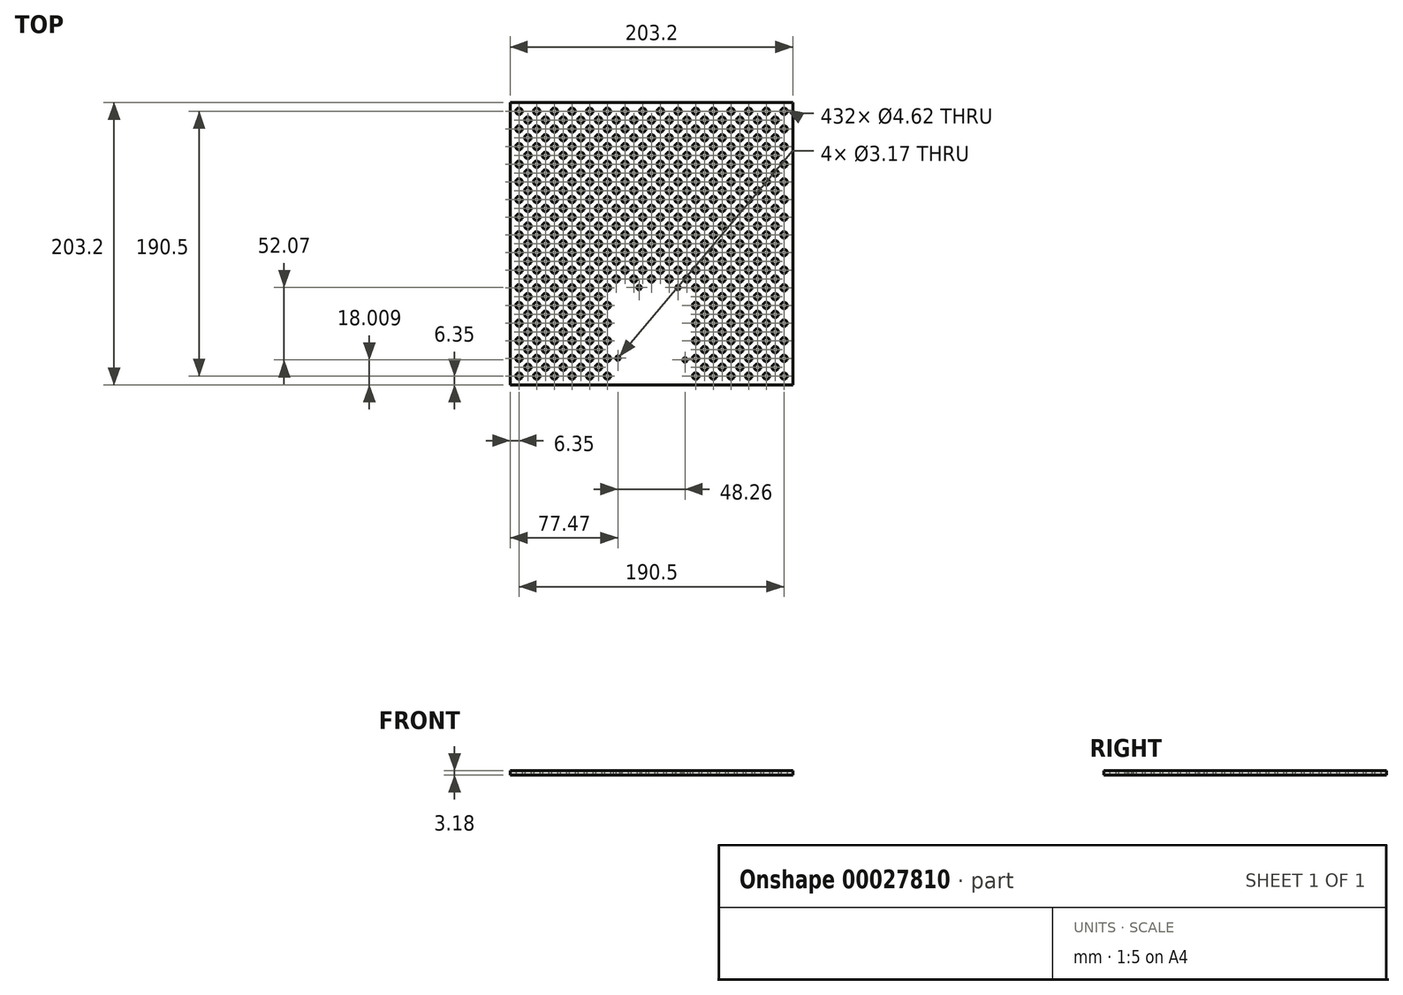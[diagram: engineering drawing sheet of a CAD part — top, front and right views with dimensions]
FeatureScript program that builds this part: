
annotation { "Feature Type Name" : "Feature", "Feature Type Description" : "" }
export const myFeature = defineFeature(function(context is Context, id is Id, definition is map)
    precondition{}
    {
        {
            var Q0;
            Q0=qCreatedBy(makeId("Top.planeOp"),FACE);
            var sketch = newSketch(context, id + "F0", { "sketchPlane" : qUnion([Q0])});
            skLineSegment(sketch, "E0", {"start": v(0, 0) * mm, "end": v(101.6, 0) * mm});
            skLineSegment(sketch, "E1", {"start": v(0, 0) * mm, "end": v(-101.6, 0) * mm});
            skLineSegment(sketch, "E2", {"start": v(-101.6, 0) * mm, "end": v(-101.6, 203.2) * mm});
            skLineSegment(sketch, "E3", {"start": v(101.6, 0) * mm, "end": v(101.6, 203.2) * mm});
            skLineSegment(sketch, "E4", {"start": v(-101.6, 203.2) * mm, "end": v(101.6, 203.2) * mm});
            skLineSegment(sketch, "E5", {"start": v(-101.6, 4.04) * mm, "end": v(101.6, 4.04) * mm, "construction": true});
            skLineSegment(sketch, "E6", {"start": v(0, 4.04) * mm, "end": v(-26.67, 4.04) * mm, "construction": true});
            skLineSegment(sketch, "E7", {"start": v(0, 4.04) * mm, "end": v(26.67, 4.04) * mm, "construction": true});
            skLineSegment(sketch, "E8", {"start": v(-101.6, 199.16) * mm, "end": v(101.6, 199.16) * mm, "construction": true});
            skLineSegment(sketch, "E9", {"start": v(-97.56, 203.2) * mm, "end": v(-97.56, 0) * mm, "construction": true});
            skCircle(sketch, "E10", {"center": v(-95.25, 196.85) * mm, "radius": 2.31 * mm});
            skCircle(sketch, "E11.0.1.0", {"center": v(-95.25, 184.15) * mm, "radius": 2.31 * mm});
            skCircle(sketch, "E11.0.2.0", {"center": v(-95.25, 171.45) * mm, "radius": 2.31 * mm});
            skCircle(sketch, "E11.0.3.0", {"center": v(-95.25, 158.75) * mm, "radius": 2.31 * mm});
            skCircle(sketch, "E11.0.4.0", {"center": v(-95.25, 146.05) * mm, "radius": 2.31 * mm});
            skCircle(sketch, "E11.0.5.0", {"center": v(-95.25, 133.35) * mm, "radius": 2.31 * mm});
            skCircle(sketch, "E11.0.6.0", {"center": v(-95.25, 120.65) * mm, "radius": 2.31 * mm});
            skCircle(sketch, "E11.0.7.0", {"center": v(-95.25, 107.95) * mm, "radius": 2.31 * mm});
            skCircle(sketch, "E11.0.8.0", {"center": v(-95.25, 95.25) * mm, "radius": 2.31 * mm});
            skCircle(sketch, "E11.0.9.0", {"center": v(-95.25, 82.55) * mm, "radius": 2.31 * mm});
            skCircle(sketch, "E11.0.10.0", {"center": v(-95.25, 69.85) * mm, "radius": 2.31 * mm});
            skCircle(sketch, "E11.0.11.0", {"center": v(-95.25, 57.15) * mm, "radius": 2.31 * mm});
            skCircle(sketch, "E11.0.12.0", {"center": v(-95.25, 44.45) * mm, "radius": 2.31 * mm});
            skCircle(sketch, "E11.0.13.0", {"center": v(-95.25, 31.75) * mm, "radius": 2.31 * mm});
            skCircle(sketch, "E11.0.14.0", {"center": v(-95.25, 19.05) * mm, "radius": 2.31 * mm});
            skCircle(sketch, "E11.0.15.0", {"center": v(-95.25, 6.35) * mm, "radius": 2.31 * mm});
            skCircle(sketch, "E11.1.0.0", {"center": v(-82.55, 196.85) * mm, "radius": 2.31 * mm});
            skCircle(sketch, "E11.1.1.0", {"center": v(-82.55, 184.15) * mm, "radius": 2.31 * mm});
            skCircle(sketch, "E11.1.2.0", {"center": v(-82.55, 171.45) * mm, "radius": 2.31 * mm});
            skCircle(sketch, "E11.1.3.0", {"center": v(-82.55, 158.75) * mm, "radius": 2.31 * mm});
            skCircle(sketch, "E11.1.4.0", {"center": v(-82.55, 146.05) * mm, "radius": 2.31 * mm});
            skCircle(sketch, "E11.1.5.0", {"center": v(-82.55, 133.35) * mm, "radius": 2.31 * mm});
            skCircle(sketch, "E11.1.6.0", {"center": v(-82.55, 120.65) * mm, "radius": 2.31 * mm});
            skCircle(sketch, "E11.1.7.0", {"center": v(-82.55, 107.95) * mm, "radius": 2.31 * mm});
            skCircle(sketch, "E11.1.8.0", {"center": v(-82.55, 95.25) * mm, "radius": 2.31 * mm});
            skCircle(sketch, "E11.1.9.0", {"center": v(-82.55, 82.55) * mm, "radius": 2.31 * mm});
            skCircle(sketch, "E11.1.10.0", {"center": v(-82.55, 69.85) * mm, "radius": 2.31 * mm});
            skCircle(sketch, "E11.1.11.0", {"center": v(-82.55, 57.15) * mm, "radius": 2.31 * mm});
            skCircle(sketch, "E11.1.12.0", {"center": v(-82.55, 44.45) * mm, "radius": 2.31 * mm});
            skCircle(sketch, "E11.1.13.0", {"center": v(-82.55, 31.75) * mm, "radius": 2.31 * mm});
            skCircle(sketch, "E11.1.14.0", {"center": v(-82.55, 19.05) * mm, "radius": 2.31 * mm});
            skCircle(sketch, "E11.1.15.0", {"center": v(-82.55, 6.35) * mm, "radius": 2.31 * mm});
            skCircle(sketch, "E11.2.0.0", {"center": v(-69.85, 196.85) * mm, "radius": 2.31 * mm});
            skCircle(sketch, "E11.2.1.0", {"center": v(-69.85, 184.15) * mm, "radius": 2.31 * mm});
            skCircle(sketch, "E11.2.2.0", {"center": v(-69.85, 171.45) * mm, "radius": 2.31 * mm});
            skCircle(sketch, "E11.2.3.0", {"center": v(-69.85, 158.75) * mm, "radius": 2.31 * mm});
            skCircle(sketch, "E11.2.4.0", {"center": v(-69.85, 146.05) * mm, "radius": 2.31 * mm});
            skCircle(sketch, "E11.2.5.0", {"center": v(-69.85, 133.35) * mm, "radius": 2.31 * mm});
            skCircle(sketch, "E11.2.6.0", {"center": v(-69.85, 120.65) * mm, "radius": 2.31 * mm});
            skCircle(sketch, "E11.2.7.0", {"center": v(-69.85, 107.95) * mm, "radius": 2.31 * mm});
            skCircle(sketch, "E11.2.8.0", {"center": v(-69.85, 95.25) * mm, "radius": 2.31 * mm});
            skCircle(sketch, "E11.2.9.0", {"center": v(-69.85, 82.55) * mm, "radius": 2.31 * mm});
            skCircle(sketch, "E11.2.10.0", {"center": v(-69.85, 69.85) * mm, "radius": 2.31 * mm});
            skCircle(sketch, "E11.2.11.0", {"center": v(-69.85, 57.15) * mm, "radius": 2.31 * mm});
            skCircle(sketch, "E11.2.12.0", {"center": v(-69.85, 44.45) * mm, "radius": 2.31 * mm});
            skCircle(sketch, "E11.2.13.0", {"center": v(-69.85, 31.75) * mm, "radius": 2.31 * mm});
            skCircle(sketch, "E11.2.14.0", {"center": v(-69.85, 19.05) * mm, "radius": 2.31 * mm});
            skCircle(sketch, "E11.2.15.0", {"center": v(-69.85, 6.35) * mm, "radius": 2.31 * mm});
            skCircle(sketch, "E11.3.0.0", {"center": v(-57.15, 196.85) * mm, "radius": 2.31 * mm});
            skCircle(sketch, "E11.3.1.0", {"center": v(-57.15, 184.15) * mm, "radius": 2.31 * mm});
            skCircle(sketch, "E11.3.2.0", {"center": v(-57.15, 171.45) * mm, "radius": 2.31 * mm});
            skCircle(sketch, "E11.3.3.0", {"center": v(-57.15, 158.75) * mm, "radius": 2.31 * mm});
            skCircle(sketch, "E11.3.4.0", {"center": v(-57.15, 146.05) * mm, "radius": 2.31 * mm});
            skCircle(sketch, "E11.3.5.0", {"center": v(-57.15, 133.35) * mm, "radius": 2.31 * mm});
            skCircle(sketch, "E11.3.6.0", {"center": v(-57.15, 120.65) * mm, "radius": 2.31 * mm});
            skCircle(sketch, "E11.3.7.0", {"center": v(-57.15, 107.95) * mm, "radius": 2.31 * mm});
            skCircle(sketch, "E11.3.8.0", {"center": v(-57.15, 95.25) * mm, "radius": 2.31 * mm});
            skCircle(sketch, "E11.3.9.0", {"center": v(-57.15, 82.55) * mm, "radius": 2.31 * mm});
            skCircle(sketch, "E11.3.10.0", {"center": v(-57.15, 69.85) * mm, "radius": 2.31 * mm});
            skCircle(sketch, "E11.3.11.0", {"center": v(-57.15, 57.15) * mm, "radius": 2.31 * mm});
            skCircle(sketch, "E11.3.12.0", {"center": v(-57.15, 44.45) * mm, "radius": 2.31 * mm});
            skCircle(sketch, "E11.3.13.0", {"center": v(-57.15, 31.75) * mm, "radius": 2.31 * mm});
            skCircle(sketch, "E11.3.14.0", {"center": v(-57.15, 19.05) * mm, "radius": 2.31 * mm});
            skCircle(sketch, "E11.3.15.0", {"center": v(-57.15, 6.35) * mm, "radius": 2.31 * mm});
            skCircle(sketch, "E11.4.0.0", {"center": v(-44.45, 196.85) * mm, "radius": 2.31 * mm});
            skCircle(sketch, "E11.4.1.0", {"center": v(-44.45, 184.15) * mm, "radius": 2.31 * mm});
            skCircle(sketch, "E11.4.2.0", {"center": v(-44.45, 171.45) * mm, "radius": 2.31 * mm});
            skCircle(sketch, "E11.4.3.0", {"center": v(-44.45, 158.75) * mm, "radius": 2.31 * mm});
            skCircle(sketch, "E11.4.4.0", {"center": v(-44.45, 146.05) * mm, "radius": 2.31 * mm});
            skCircle(sketch, "E11.4.5.0", {"center": v(-44.45, 133.35) * mm, "radius": 2.31 * mm});
            skCircle(sketch, "E11.4.6.0", {"center": v(-44.45, 120.65) * mm, "radius": 2.31 * mm});
            skCircle(sketch, "E11.4.7.0", {"center": v(-44.45, 107.95) * mm, "radius": 2.31 * mm});
            skCircle(sketch, "E11.4.8.0", {"center": v(-44.45, 95.25) * mm, "radius": 2.31 * mm});
            skCircle(sketch, "E11.4.9.0", {"center": v(-44.45, 82.55) * mm, "radius": 2.31 * mm});
            skCircle(sketch, "E11.4.10.0", {"center": v(-44.45, 69.85) * mm, "radius": 2.31 * mm});
            skCircle(sketch, "E11.4.11.0", {"center": v(-44.45, 57.15) * mm, "radius": 2.31 * mm});
            skCircle(sketch, "E11.4.12.0", {"center": v(-44.45, 44.45) * mm, "radius": 2.31 * mm});
            skCircle(sketch, "E11.4.13.0", {"center": v(-44.45, 31.75) * mm, "radius": 2.31 * mm});
            skCircle(sketch, "E11.4.14.0", {"center": v(-44.45, 19.05) * mm, "radius": 2.31 * mm});
            skCircle(sketch, "E11.4.15.0", {"center": v(-44.45, 6.35) * mm, "radius": 2.31 * mm});
            skCircle(sketch, "E11.5.0.0", {"center": v(-31.75, 196.85) * mm, "radius": 2.31 * mm});
            skCircle(sketch, "E11.5.1.0", {"center": v(-31.75, 184.15) * mm, "radius": 2.31 * mm});
            skCircle(sketch, "E11.5.2.0", {"center": v(-31.75, 171.45) * mm, "radius": 2.31 * mm});
            skCircle(sketch, "E11.5.3.0", {"center": v(-31.75, 158.75) * mm, "radius": 2.31 * mm});
            skCircle(sketch, "E11.5.4.0", {"center": v(-31.75, 146.05) * mm, "radius": 2.31 * mm});
            skCircle(sketch, "E11.5.5.0", {"center": v(-31.75, 133.35) * mm, "radius": 2.31 * mm});
            skCircle(sketch, "E11.5.6.0", {"center": v(-31.75, 120.65) * mm, "radius": 2.31 * mm});
            skCircle(sketch, "E11.5.7.0", {"center": v(-31.75, 107.95) * mm, "radius": 2.31 * mm});
            skCircle(sketch, "E11.5.8.0", {"center": v(-31.75, 95.25) * mm, "radius": 2.31 * mm});
            skCircle(sketch, "E11.5.9.0", {"center": v(-31.75, 82.55) * mm, "radius": 2.31 * mm});
            skCircle(sketch, "E11.5.10.0", {"center": v(-31.75, 69.85) * mm, "radius": 2.31 * mm});
            skCircle(sketch, "E11.5.11.0", {"center": v(-31.75, 57.15) * mm, "radius": 2.31 * mm});
            skCircle(sketch, "E11.5.12.0", {"center": v(-31.75, 44.45) * mm, "radius": 2.31 * mm});
            skCircle(sketch, "E11.5.13.0", {"center": v(-31.75, 31.75) * mm, "radius": 2.31 * mm});
            skCircle(sketch, "E11.5.14.0", {"center": v(-31.75, 19.05) * mm, "radius": 2.31 * mm});
            skCircle(sketch, "E11.5.15.0", {"center": v(-31.75, 6.35) * mm, "radius": 2.31 * mm});
            skCircle(sketch, "E11.6.0.0", {"center": v(-19.05, 196.85) * mm, "radius": 2.31 * mm});
            skCircle(sketch, "E11.6.1.0", {"center": v(-19.05, 184.15) * mm, "radius": 2.31 * mm});
            skCircle(sketch, "E11.6.2.0", {"center": v(-19.05, 171.45) * mm, "radius": 2.31 * mm});
            skCircle(sketch, "E11.6.3.0", {"center": v(-19.05, 158.75) * mm, "radius": 2.31 * mm});
            skCircle(sketch, "E11.6.4.0", {"center": v(-19.05, 146.05) * mm, "radius": 2.31 * mm});
            skCircle(sketch, "E11.6.5.0", {"center": v(-19.05, 133.35) * mm, "radius": 2.31 * mm});
            skCircle(sketch, "E11.6.6.0", {"center": v(-19.05, 120.65) * mm, "radius": 2.31 * mm});
            skCircle(sketch, "E11.6.7.0", {"center": v(-19.05, 107.95) * mm, "radius": 2.31 * mm});
            skCircle(sketch, "E11.6.8.0", {"center": v(-19.05, 95.25) * mm, "radius": 2.31 * mm});
            skCircle(sketch, "E11.6.9.0", {"center": v(-19.05, 82.55) * mm, "radius": 2.31 * mm});
            skCircle(sketch, "E11.7.0.0", {"center": v(-6.35, 196.85) * mm, "radius": 2.31 * mm});
            skCircle(sketch, "E11.7.1.0", {"center": v(-6.35, 184.15) * mm, "radius": 2.31 * mm});
            skCircle(sketch, "E11.7.2.0", {"center": v(-6.35, 171.45) * mm, "radius": 2.31 * mm});
            skCircle(sketch, "E11.7.3.0", {"center": v(-6.35, 158.75) * mm, "radius": 2.31 * mm});
            skCircle(sketch, "E11.7.4.0", {"center": v(-6.35, 146.05) * mm, "radius": 2.31 * mm});
            skCircle(sketch, "E11.7.5.0", {"center": v(-6.35, 133.35) * mm, "radius": 2.31 * mm});
            skCircle(sketch, "E11.7.6.0", {"center": v(-6.35, 120.65) * mm, "radius": 2.31 * mm});
            skCircle(sketch, "E11.7.7.0", {"center": v(-6.35, 107.95) * mm, "radius": 2.31 * mm});
            skCircle(sketch, "E11.7.8.0", {"center": v(-6.35, 95.25) * mm, "radius": 2.31 * mm});
            skCircle(sketch, "E11.7.9.0", {"center": v(-6.35, 82.55) * mm, "radius": 2.31 * mm});
            skCircle(sketch, "E11.8.0.0", {"center": v(6.35, 196.85) * mm, "radius": 2.31 * mm});
            skCircle(sketch, "E11.8.1.0", {"center": v(6.35, 184.15) * mm, "radius": 2.31 * mm});
            skCircle(sketch, "E11.8.2.0", {"center": v(6.35, 171.45) * mm, "radius": 2.31 * mm});
            skCircle(sketch, "E11.8.3.0", {"center": v(6.35, 158.75) * mm, "radius": 2.31 * mm});
            skCircle(sketch, "E11.8.4.0", {"center": v(6.35, 146.05) * mm, "radius": 2.31 * mm});
            skCircle(sketch, "E11.8.5.0", {"center": v(6.35, 133.35) * mm, "radius": 2.31 * mm});
            skCircle(sketch, "E11.8.6.0", {"center": v(6.35, 120.65) * mm, "radius": 2.31 * mm});
            skCircle(sketch, "E11.8.7.0", {"center": v(6.35, 107.95) * mm, "radius": 2.31 * mm});
            skCircle(sketch, "E11.8.8.0", {"center": v(6.35, 95.25) * mm, "radius": 2.31 * mm});
            skCircle(sketch, "E11.8.9.0", {"center": v(6.35, 82.55) * mm, "radius": 2.31 * mm});
            skCircle(sketch, "E11.9.0.0", {"center": v(19.05, 196.85) * mm, "radius": 2.31 * mm});
            skCircle(sketch, "E11.9.1.0", {"center": v(19.05, 184.15) * mm, "radius": 2.31 * mm});
            skCircle(sketch, "E11.9.2.0", {"center": v(19.05, 171.45) * mm, "radius": 2.31 * mm});
            skCircle(sketch, "E11.9.3.0", {"center": v(19.05, 158.75) * mm, "radius": 2.31 * mm});
            skCircle(sketch, "E11.9.4.0", {"center": v(19.05, 146.05) * mm, "radius": 2.31 * mm});
            skCircle(sketch, "E11.9.5.0", {"center": v(19.05, 133.35) * mm, "radius": 2.31 * mm});
            skCircle(sketch, "E11.9.6.0", {"center": v(19.05, 120.65) * mm, "radius": 2.31 * mm});
            skCircle(sketch, "E11.9.7.0", {"center": v(19.05, 107.95) * mm, "radius": 2.31 * mm});
            skCircle(sketch, "E11.9.8.0", {"center": v(19.05, 95.25) * mm, "radius": 2.31 * mm});
            skCircle(sketch, "E11.9.9.0", {"center": v(19.05, 82.55) * mm, "radius": 2.31 * mm});
            skCircle(sketch, "E11.10.0.0", {"center": v(31.75, 196.85) * mm, "radius": 2.31 * mm});
            skCircle(sketch, "E11.10.1.0", {"center": v(31.75, 184.15) * mm, "radius": 2.31 * mm});
            skCircle(sketch, "E11.10.2.0", {"center": v(31.75, 171.45) * mm, "radius": 2.31 * mm});
            skCircle(sketch, "E11.10.3.0", {"center": v(31.75, 158.75) * mm, "radius": 2.31 * mm});
            skCircle(sketch, "E11.10.4.0", {"center": v(31.75, 146.05) * mm, "radius": 2.31 * mm});
            skCircle(sketch, "E11.10.5.0", {"center": v(31.75, 133.35) * mm, "radius": 2.31 * mm});
            skCircle(sketch, "E11.10.6.0", {"center": v(31.75, 120.65) * mm, "radius": 2.31 * mm});
            skCircle(sketch, "E11.10.7.0", {"center": v(31.75, 107.95) * mm, "radius": 2.31 * mm});
            skCircle(sketch, "E11.10.8.0", {"center": v(31.75, 95.25) * mm, "radius": 2.31 * mm});
            skCircle(sketch, "E11.10.9.0", {"center": v(31.75, 82.55) * mm, "radius": 2.31 * mm});
            skCircle(sketch, "E11.10.10.0", {"center": v(31.75, 69.85) * mm, "radius": 2.31 * mm});
            skCircle(sketch, "E11.10.11.0", {"center": v(31.75, 57.15) * mm, "radius": 2.31 * mm});
            skCircle(sketch, "E11.10.12.0", {"center": v(31.75, 44.45) * mm, "radius": 2.31 * mm});
            skCircle(sketch, "E11.10.13.0", {"center": v(31.75, 31.75) * mm, "radius": 2.31 * mm});
            skCircle(sketch, "E11.10.14.0", {"center": v(31.75, 19.05) * mm, "radius": 2.31 * mm});
            skCircle(sketch, "E11.10.15.0", {"center": v(31.75, 6.35) * mm, "radius": 2.31 * mm});
            skCircle(sketch, "E11.11.0.0", {"center": v(44.45, 196.85) * mm, "radius": 2.31 * mm});
            skCircle(sketch, "E11.11.1.0", {"center": v(44.45, 184.15) * mm, "radius": 2.31 * mm});
            skCircle(sketch, "E11.11.2.0", {"center": v(44.45, 171.45) * mm, "radius": 2.31 * mm});
            skCircle(sketch, "E11.11.3.0", {"center": v(44.45, 158.75) * mm, "radius": 2.31 * mm});
            skCircle(sketch, "E11.11.4.0", {"center": v(44.45, 146.05) * mm, "radius": 2.31 * mm});
            skCircle(sketch, "E11.11.5.0", {"center": v(44.45, 133.35) * mm, "radius": 2.31 * mm});
            skCircle(sketch, "E11.11.6.0", {"center": v(44.45, 120.65) * mm, "radius": 2.31 * mm});
            skCircle(sketch, "E11.11.7.0", {"center": v(44.45, 107.95) * mm, "radius": 2.31 * mm});
            skCircle(sketch, "E11.11.8.0", {"center": v(44.45, 95.25) * mm, "radius": 2.31 * mm});
            skCircle(sketch, "E11.11.9.0", {"center": v(44.45, 82.55) * mm, "radius": 2.31 * mm});
            skCircle(sketch, "E11.11.10.0", {"center": v(44.45, 69.85) * mm, "radius": 2.31 * mm});
            skCircle(sketch, "E11.11.11.0", {"center": v(44.45, 57.15) * mm, "radius": 2.31 * mm});
            skCircle(sketch, "E11.11.12.0", {"center": v(44.45, 44.45) * mm, "radius": 2.31 * mm});
            skCircle(sketch, "E11.11.13.0", {"center": v(44.45, 31.75) * mm, "radius": 2.31 * mm});
            skCircle(sketch, "E11.11.14.0", {"center": v(44.45, 19.05) * mm, "radius": 2.31 * mm});
            skCircle(sketch, "E11.11.15.0", {"center": v(44.45, 6.35) * mm, "radius": 2.31 * mm});
            skCircle(sketch, "E11.12.0.0", {"center": v(57.15, 196.85) * mm, "radius": 2.31 * mm});
            skCircle(sketch, "E11.12.1.0", {"center": v(57.15, 184.15) * mm, "radius": 2.31 * mm});
            skCircle(sketch, "E11.12.2.0", {"center": v(57.15, 171.45) * mm, "radius": 2.31 * mm});
            skCircle(sketch, "E11.12.3.0", {"center": v(57.15, 158.75) * mm, "radius": 2.31 * mm});
            skCircle(sketch, "E11.12.4.0", {"center": v(57.15, 146.05) * mm, "radius": 2.31 * mm});
            skCircle(sketch, "E11.12.5.0", {"center": v(57.15, 133.35) * mm, "radius": 2.31 * mm});
            skCircle(sketch, "E11.12.6.0", {"center": v(57.15, 120.65) * mm, "radius": 2.31 * mm});
            skCircle(sketch, "E11.12.7.0", {"center": v(57.15, 107.95) * mm, "radius": 2.31 * mm});
            skCircle(sketch, "E11.12.8.0", {"center": v(57.15, 95.25) * mm, "radius": 2.31 * mm});
            skCircle(sketch, "E11.12.9.0", {"center": v(57.15, 82.55) * mm, "radius": 2.31 * mm});
            skCircle(sketch, "E11.12.10.0", {"center": v(57.15, 69.85) * mm, "radius": 2.31 * mm});
            skCircle(sketch, "E11.12.11.0", {"center": v(57.15, 57.15) * mm, "radius": 2.31 * mm});
            skCircle(sketch, "E11.12.12.0", {"center": v(57.15, 44.45) * mm, "radius": 2.31 * mm});
            skCircle(sketch, "E11.12.13.0", {"center": v(57.15, 31.75) * mm, "radius": 2.31 * mm});
            skCircle(sketch, "E11.12.14.0", {"center": v(57.15, 19.05) * mm, "radius": 2.31 * mm});
            skCircle(sketch, "E11.12.15.0", {"center": v(57.15, 6.35) * mm, "radius": 2.31 * mm});
            skCircle(sketch, "E11.13.0.0", {"center": v(69.85, 196.85) * mm, "radius": 2.31 * mm});
            skCircle(sketch, "E11.13.1.0", {"center": v(69.85, 184.15) * mm, "radius": 2.31 * mm});
            skCircle(sketch, "E11.13.2.0", {"center": v(69.85, 171.45) * mm, "radius": 2.31 * mm});
            skCircle(sketch, "E11.13.3.0", {"center": v(69.85, 158.75) * mm, "radius": 2.31 * mm});
            skCircle(sketch, "E11.13.4.0", {"center": v(69.85, 146.05) * mm, "radius": 2.31 * mm});
            skCircle(sketch, "E11.13.5.0", {"center": v(69.85, 133.35) * mm, "radius": 2.31 * mm});
            skCircle(sketch, "E11.13.6.0", {"center": v(69.85, 120.65) * mm, "radius": 2.31 * mm});
            skCircle(sketch, "E11.13.7.0", {"center": v(69.85, 107.95) * mm, "radius": 2.31 * mm});
            skCircle(sketch, "E11.13.8.0", {"center": v(69.85, 95.25) * mm, "radius": 2.31 * mm});
            skCircle(sketch, "E11.13.9.0", {"center": v(69.85, 82.55) * mm, "radius": 2.31 * mm});
            skCircle(sketch, "E11.13.10.0", {"center": v(69.85, 69.85) * mm, "radius": 2.31 * mm});
            skCircle(sketch, "E11.13.11.0", {"center": v(69.85, 57.15) * mm, "radius": 2.31 * mm});
            skCircle(sketch, "E11.13.12.0", {"center": v(69.85, 44.45) * mm, "radius": 2.31 * mm});
            skCircle(sketch, "E11.13.13.0", {"center": v(69.85, 31.75) * mm, "radius": 2.31 * mm});
            skCircle(sketch, "E11.13.14.0", {"center": v(69.85, 19.05) * mm, "radius": 2.31 * mm});
            skCircle(sketch, "E11.13.15.0", {"center": v(69.85, 6.35) * mm, "radius": 2.31 * mm});
            skCircle(sketch, "E11.14.0.0", {"center": v(82.55, 196.85) * mm, "radius": 2.31 * mm});
            skCircle(sketch, "E11.14.1.0", {"center": v(82.55, 184.15) * mm, "radius": 2.31 * mm});
            skCircle(sketch, "E11.14.2.0", {"center": v(82.55, 171.45) * mm, "radius": 2.31 * mm});
            skCircle(sketch, "E11.14.3.0", {"center": v(82.55, 158.75) * mm, "radius": 2.31 * mm});
            skCircle(sketch, "E11.14.4.0", {"center": v(82.55, 146.05) * mm, "radius": 2.31 * mm});
            skCircle(sketch, "E11.14.5.0", {"center": v(82.55, 133.35) * mm, "radius": 2.31 * mm});
            skCircle(sketch, "E11.14.6.0", {"center": v(82.55, 120.65) * mm, "radius": 2.31 * mm});
            skCircle(sketch, "E11.14.7.0", {"center": v(82.55, 107.95) * mm, "radius": 2.31 * mm});
            skCircle(sketch, "E11.14.8.0", {"center": v(82.55, 95.25) * mm, "radius": 2.31 * mm});
            skCircle(sketch, "E11.14.9.0", {"center": v(82.55, 82.55) * mm, "radius": 2.31 * mm});
            skCircle(sketch, "E11.14.10.0", {"center": v(82.55, 69.85) * mm, "radius": 2.31 * mm});
            skCircle(sketch, "E11.14.11.0", {"center": v(82.55, 57.15) * mm, "radius": 2.31 * mm});
            skCircle(sketch, "E11.14.12.0", {"center": v(82.55, 44.45) * mm, "radius": 2.31 * mm});
            skCircle(sketch, "E11.14.13.0", {"center": v(82.55, 31.75) * mm, "radius": 2.31 * mm});
            skCircle(sketch, "E11.14.14.0", {"center": v(82.55, 19.05) * mm, "radius": 2.31 * mm});
            skCircle(sketch, "E11.14.15.0", {"center": v(82.55, 6.35) * mm, "radius": 2.31 * mm});
            skCircle(sketch, "E11.15.0.0", {"center": v(95.25, 196.85) * mm, "radius": 2.31 * mm});
            skCircle(sketch, "E11.15.1.0", {"center": v(95.25, 184.15) * mm, "radius": 2.31 * mm});
            skCircle(sketch, "E11.15.2.0", {"center": v(95.25, 171.45) * mm, "radius": 2.31 * mm});
            skCircle(sketch, "E11.15.3.0", {"center": v(95.25, 158.75) * mm, "radius": 2.31 * mm});
            skCircle(sketch, "E11.15.4.0", {"center": v(95.25, 146.05) * mm, "radius": 2.31 * mm});
            skCircle(sketch, "E11.15.5.0", {"center": v(95.25, 133.35) * mm, "radius": 2.31 * mm});
            skCircle(sketch, "E11.15.6.0", {"center": v(95.25, 120.65) * mm, "radius": 2.31 * mm});
            skCircle(sketch, "E11.15.7.0", {"center": v(95.25, 107.95) * mm, "radius": 2.31 * mm});
            skCircle(sketch, "E11.15.8.0", {"center": v(95.25, 95.25) * mm, "radius": 2.31 * mm});
            skCircle(sketch, "E11.15.9.0", {"center": v(95.25, 82.55) * mm, "radius": 2.31 * mm});
            skCircle(sketch, "E11.15.10.0", {"center": v(95.25, 69.85) * mm, "radius": 2.31 * mm});
            skCircle(sketch, "E11.15.11.0", {"center": v(95.25, 57.15) * mm, "radius": 2.31 * mm});
            skCircle(sketch, "E11.15.12.0", {"center": v(95.25, 44.45) * mm, "radius": 2.31 * mm});
            skCircle(sketch, "E11.15.13.0", {"center": v(95.25, 31.75) * mm, "radius": 2.31 * mm});
            skCircle(sketch, "E11.15.14.0", {"center": v(95.25, 19.05) * mm, "radius": 2.31 * mm});
            skCircle(sketch, "E11.15.15.0", {"center": v(95.25, 6.35) * mm, "radius": 2.31 * mm});
            skLineSegment(sketch, "E11.direction1", {"start": v(-95.25, 196.85) * mm, "end": v(-82.55, 196.85) * mm, "construction": true});
            skLineSegment(sketch, "E11.direction2", {"start": v(-95.25, 196.85) * mm, "end": v(-95.25, 184.15) * mm, "construction": true});
            skCircle(sketch, "E12", {"center": v(-88.9, 190.5) * mm, "radius": 2.31 * mm});
            skCircle(sketch, "E13.0.1.0", {"center": v(-88.9, 177.8) * mm, "radius": 2.31 * mm});
            skCircle(sketch, "E13.0.2.0", {"center": v(-88.9, 165.1) * mm, "radius": 2.31 * mm});
            skCircle(sketch, "E13.0.3.0", {"center": v(-88.9, 152.4) * mm, "radius": 2.31 * mm});
            skCircle(sketch, "E13.0.4.0", {"center": v(-88.9, 139.7) * mm, "radius": 2.31 * mm});
            skCircle(sketch, "E13.0.5.0", {"center": v(-88.9, 127) * mm, "radius": 2.31 * mm});
            skCircle(sketch, "E13.0.6.0", {"center": v(-88.9, 114.3) * mm, "radius": 2.31 * mm});
            skCircle(sketch, "E13.0.7.0", {"center": v(-88.9, 101.6) * mm, "radius": 2.31 * mm});
            skCircle(sketch, "E13.0.8.0", {"center": v(-88.9, 88.9) * mm, "radius": 2.31 * mm});
            skCircle(sketch, "E13.0.9.0", {"center": v(-88.9, 76.2) * mm, "radius": 2.31 * mm});
            skCircle(sketch, "E13.0.10.0", {"center": v(-88.9, 63.5) * mm, "radius": 2.31 * mm});
            skCircle(sketch, "E13.0.11.0", {"center": v(-88.9, 50.8) * mm, "radius": 2.31 * mm});
            skCircle(sketch, "E13.0.12.0", {"center": v(-88.9, 38.1) * mm, "radius": 2.31 * mm});
            skCircle(sketch, "E13.0.13.0", {"center": v(-88.9, 25.4) * mm, "radius": 2.31 * mm});
            skCircle(sketch, "E13.0.14.0", {"center": v(-88.9, 12.7) * mm, "radius": 2.31 * mm});
            skCircle(sketch, "E13.1.0.0", {"center": v(-76.2, 190.5) * mm, "radius": 2.31 * mm});
            skCircle(sketch, "E13.1.1.0", {"center": v(-76.2, 177.8) * mm, "radius": 2.31 * mm});
            skCircle(sketch, "E13.1.2.0", {"center": v(-76.2, 165.1) * mm, "radius": 2.31 * mm});
            skCircle(sketch, "E13.1.3.0", {"center": v(-76.2, 152.4) * mm, "radius": 2.31 * mm});
            skCircle(sketch, "E13.1.4.0", {"center": v(-76.2, 139.7) * mm, "radius": 2.31 * mm});
            skCircle(sketch, "E13.1.5.0", {"center": v(-76.2, 127) * mm, "radius": 2.31 * mm});
            skCircle(sketch, "E13.1.6.0", {"center": v(-76.2, 114.3) * mm, "radius": 2.31 * mm});
            skCircle(sketch, "E13.1.7.0", {"center": v(-76.2, 101.6) * mm, "radius": 2.31 * mm});
            skCircle(sketch, "E13.1.8.0", {"center": v(-76.2, 88.9) * mm, "radius": 2.31 * mm});
            skCircle(sketch, "E13.1.9.0", {"center": v(-76.2, 76.2) * mm, "radius": 2.31 * mm});
            skCircle(sketch, "E13.1.10.0", {"center": v(-76.2, 63.5) * mm, "radius": 2.31 * mm});
            skCircle(sketch, "E13.1.11.0", {"center": v(-76.2, 50.8) * mm, "radius": 2.31 * mm});
            skCircle(sketch, "E13.1.12.0", {"center": v(-76.2, 38.1) * mm, "radius": 2.31 * mm});
            skCircle(sketch, "E13.1.13.0", {"center": v(-76.2, 25.4) * mm, "radius": 2.31 * mm});
            skCircle(sketch, "E13.1.14.0", {"center": v(-76.2, 12.7) * mm, "radius": 2.31 * mm});
            skCircle(sketch, "E13.2.0.0", {"center": v(-63.5, 190.5) * mm, "radius": 2.31 * mm});
            skCircle(sketch, "E13.2.1.0", {"center": v(-63.5, 177.8) * mm, "radius": 2.31 * mm});
            skCircle(sketch, "E13.2.2.0", {"center": v(-63.5, 165.1) * mm, "radius": 2.31 * mm});
            skCircle(sketch, "E13.2.3.0", {"center": v(-63.5, 152.4) * mm, "radius": 2.31 * mm});
            skCircle(sketch, "E13.2.4.0", {"center": v(-63.5, 139.7) * mm, "radius": 2.31 * mm});
            skCircle(sketch, "E13.2.5.0", {"center": v(-63.5, 127) * mm, "radius": 2.31 * mm});
            skCircle(sketch, "E13.2.6.0", {"center": v(-63.5, 114.3) * mm, "radius": 2.31 * mm});
            skCircle(sketch, "E13.2.7.0", {"center": v(-63.5, 101.6) * mm, "radius": 2.31 * mm});
            skCircle(sketch, "E13.2.8.0", {"center": v(-63.5, 88.9) * mm, "radius": 2.31 * mm});
            skCircle(sketch, "E13.2.9.0", {"center": v(-63.5, 76.2) * mm, "radius": 2.31 * mm});
            skCircle(sketch, "E13.2.10.0", {"center": v(-63.5, 63.5) * mm, "radius": 2.31 * mm});
            skCircle(sketch, "E13.2.11.0", {"center": v(-63.5, 50.8) * mm, "radius": 2.31 * mm});
            skCircle(sketch, "E13.2.12.0", {"center": v(-63.5, 38.1) * mm, "radius": 2.31 * mm});
            skCircle(sketch, "E13.2.13.0", {"center": v(-63.5, 25.4) * mm, "radius": 2.31 * mm});
            skCircle(sketch, "E13.2.14.0", {"center": v(-63.5, 12.7) * mm, "radius": 2.31 * mm});
            skCircle(sketch, "E13.3.0.0", {"center": v(-50.8, 190.5) * mm, "radius": 2.31 * mm});
            skCircle(sketch, "E13.3.1.0", {"center": v(-50.8, 177.8) * mm, "radius": 2.31 * mm});
            skCircle(sketch, "E13.3.2.0", {"center": v(-50.8, 165.1) * mm, "radius": 2.31 * mm});
            skCircle(sketch, "E13.3.3.0", {"center": v(-50.8, 152.4) * mm, "radius": 2.31 * mm});
            skCircle(sketch, "E13.3.4.0", {"center": v(-50.8, 139.7) * mm, "radius": 2.31 * mm});
            skCircle(sketch, "E13.3.5.0", {"center": v(-50.8, 127) * mm, "radius": 2.31 * mm});
            skCircle(sketch, "E13.3.6.0", {"center": v(-50.8, 114.3) * mm, "radius": 2.31 * mm});
            skCircle(sketch, "E13.3.7.0", {"center": v(-50.8, 101.6) * mm, "radius": 2.31 * mm});
            skCircle(sketch, "E13.3.8.0", {"center": v(-50.8, 88.9) * mm, "radius": 2.31 * mm});
            skCircle(sketch, "E13.3.9.0", {"center": v(-50.8, 76.2) * mm, "radius": 2.31 * mm});
            skCircle(sketch, "E13.3.10.0", {"center": v(-50.8, 63.5) * mm, "radius": 2.31 * mm});
            skCircle(sketch, "E13.3.11.0", {"center": v(-50.8, 50.8) * mm, "radius": 2.31 * mm});
            skCircle(sketch, "E13.3.12.0", {"center": v(-50.8, 38.1) * mm, "radius": 2.31 * mm});
            skCircle(sketch, "E13.3.13.0", {"center": v(-50.8, 25.4) * mm, "radius": 2.31 * mm});
            skCircle(sketch, "E13.3.14.0", {"center": v(-50.8, 12.7) * mm, "radius": 2.31 * mm});
            skCircle(sketch, "E13.4.0.0", {"center": v(-38.1, 190.5) * mm, "radius": 2.31 * mm});
            skCircle(sketch, "E13.4.1.0", {"center": v(-38.1, 177.8) * mm, "radius": 2.31 * mm});
            skCircle(sketch, "E13.4.2.0", {"center": v(-38.1, 165.1) * mm, "radius": 2.31 * mm});
            skCircle(sketch, "E13.4.3.0", {"center": v(-38.1, 152.4) * mm, "radius": 2.31 * mm});
            skCircle(sketch, "E13.4.4.0", {"center": v(-38.1, 139.7) * mm, "radius": 2.31 * mm});
            skCircle(sketch, "E13.4.5.0", {"center": v(-38.1, 127) * mm, "radius": 2.31 * mm});
            skCircle(sketch, "E13.4.6.0", {"center": v(-38.1, 114.3) * mm, "radius": 2.31 * mm});
            skCircle(sketch, "E13.4.7.0", {"center": v(-38.1, 101.6) * mm, "radius": 2.31 * mm});
            skCircle(sketch, "E13.4.8.0", {"center": v(-38.1, 88.9) * mm, "radius": 2.31 * mm});
            skCircle(sketch, "E13.4.9.0", {"center": v(-38.1, 76.2) * mm, "radius": 2.31 * mm});
            skCircle(sketch, "E13.4.10.0", {"center": v(-38.1, 63.5) * mm, "radius": 2.31 * mm});
            skCircle(sketch, "E13.4.11.0", {"center": v(-38.1, 50.8) * mm, "radius": 2.31 * mm});
            skCircle(sketch, "E13.4.12.0", {"center": v(-38.1, 38.1) * mm, "radius": 2.31 * mm});
            skCircle(sketch, "E13.4.13.0", {"center": v(-38.1, 25.4) * mm, "radius": 2.31 * mm});
            skCircle(sketch, "E13.4.14.0", {"center": v(-38.1, 12.7) * mm, "radius": 2.31 * mm});
            skCircle(sketch, "E13.5.0.0", {"center": v(-25.4, 190.5) * mm, "radius": 2.31 * mm});
            skCircle(sketch, "E13.5.1.0", {"center": v(-25.4, 177.8) * mm, "radius": 2.31 * mm});
            skCircle(sketch, "E13.5.2.0", {"center": v(-25.4, 165.1) * mm, "radius": 2.31 * mm});
            skCircle(sketch, "E13.5.3.0", {"center": v(-25.4, 152.4) * mm, "radius": 2.31 * mm});
            skCircle(sketch, "E13.5.4.0", {"center": v(-25.4, 139.7) * mm, "radius": 2.31 * mm});
            skCircle(sketch, "E13.5.5.0", {"center": v(-25.4, 127) * mm, "radius": 2.31 * mm});
            skCircle(sketch, "E13.5.6.0", {"center": v(-25.4, 114.3) * mm, "radius": 2.31 * mm});
            skCircle(sketch, "E13.5.7.0", {"center": v(-25.4, 101.6) * mm, "radius": 2.31 * mm});
            skCircle(sketch, "E13.5.8.0", {"center": v(-25.4, 88.9) * mm, "radius": 2.31 * mm});
            skCircle(sketch, "E13.5.9.0", {"center": v(-25.4, 76.2) * mm, "radius": 2.31 * mm});
            skCircle(sketch, "E13.6.0.0", {"center": v(-12.7, 190.5) * mm, "radius": 2.31 * mm});
            skCircle(sketch, "E13.6.1.0", {"center": v(-12.7, 177.8) * mm, "radius": 2.31 * mm});
            skCircle(sketch, "E13.6.2.0", {"center": v(-12.7, 165.1) * mm, "radius": 2.31 * mm});
            skCircle(sketch, "E13.6.3.0", {"center": v(-12.7, 152.4) * mm, "radius": 2.31 * mm});
            skCircle(sketch, "E13.6.4.0", {"center": v(-12.7, 139.7) * mm, "radius": 2.31 * mm});
            skCircle(sketch, "E13.6.5.0", {"center": v(-12.7, 127) * mm, "radius": 2.31 * mm});
            skCircle(sketch, "E13.6.6.0", {"center": v(-12.7, 114.3) * mm, "radius": 2.31 * mm});
            skCircle(sketch, "E13.6.7.0", {"center": v(-12.7, 101.6) * mm, "radius": 2.31 * mm});
            skCircle(sketch, "E13.6.8.0", {"center": v(-12.7, 88.9) * mm, "radius": 2.31 * mm});
            skCircle(sketch, "E13.6.9.0", {"center": v(-12.7, 76.2) * mm, "radius": 2.31 * mm});
            skCircle(sketch, "E13.7.0.0", {"center": v(0, 190.5) * mm, "radius": 2.31 * mm});
            skCircle(sketch, "E13.7.1.0", {"center": v(0, 177.8) * mm, "radius": 2.31 * mm});
            skCircle(sketch, "E13.7.2.0", {"center": v(0, 165.1) * mm, "radius": 2.31 * mm});
            skCircle(sketch, "E13.7.3.0", {"center": v(0, 152.4) * mm, "radius": 2.31 * mm});
            skCircle(sketch, "E13.7.4.0", {"center": v(0, 139.7) * mm, "radius": 2.31 * mm});
            skCircle(sketch, "E13.7.5.0", {"center": v(0, 127) * mm, "radius": 2.31 * mm});
            skCircle(sketch, "E13.7.6.0", {"center": v(0, 114.3) * mm, "radius": 2.31 * mm});
            skCircle(sketch, "E13.7.7.0", {"center": v(0, 101.6) * mm, "radius": 2.31 * mm});
            skCircle(sketch, "E13.7.8.0", {"center": v(0, 88.9) * mm, "radius": 2.31 * mm});
            skCircle(sketch, "E13.7.9.0", {"center": v(0, 76.2) * mm, "radius": 2.31 * mm});
            skCircle(sketch, "E13.8.0.0", {"center": v(12.7, 190.5) * mm, "radius": 2.31 * mm});
            skCircle(sketch, "E13.8.1.0", {"center": v(12.7, 177.8) * mm, "radius": 2.31 * mm});
            skCircle(sketch, "E13.8.2.0", {"center": v(12.7, 165.1) * mm, "radius": 2.31 * mm});
            skCircle(sketch, "E13.8.3.0", {"center": v(12.7, 152.4) * mm, "radius": 2.31 * mm});
            skCircle(sketch, "E13.8.4.0", {"center": v(12.7, 139.7) * mm, "radius": 2.31 * mm});
            skCircle(sketch, "E13.8.5.0", {"center": v(12.7, 127) * mm, "radius": 2.31 * mm});
            skCircle(sketch, "E13.8.6.0", {"center": v(12.7, 114.3) * mm, "radius": 2.31 * mm});
            skCircle(sketch, "E13.8.7.0", {"center": v(12.7, 101.6) * mm, "radius": 2.31 * mm});
            skCircle(sketch, "E13.8.8.0", {"center": v(12.7, 88.9) * mm, "radius": 2.31 * mm});
            skCircle(sketch, "E13.8.9.0", {"center": v(12.7, 76.2) * mm, "radius": 2.31 * mm});
            skCircle(sketch, "E13.9.0.0", {"center": v(25.4, 190.5) * mm, "radius": 2.31 * mm});
            skCircle(sketch, "E13.9.1.0", {"center": v(25.4, 177.8) * mm, "radius": 2.31 * mm});
            skCircle(sketch, "E13.9.2.0", {"center": v(25.4, 165.1) * mm, "radius": 2.31 * mm});
            skCircle(sketch, "E13.9.3.0", {"center": v(25.4, 152.4) * mm, "radius": 2.31 * mm});
            skCircle(sketch, "E13.9.4.0", {"center": v(25.4, 139.7) * mm, "radius": 2.31 * mm});
            skCircle(sketch, "E13.9.5.0", {"center": v(25.4, 127) * mm, "radius": 2.31 * mm});
            skCircle(sketch, "E13.9.6.0", {"center": v(25.4, 114.3) * mm, "radius": 2.31 * mm});
            skCircle(sketch, "E13.9.7.0", {"center": v(25.4, 101.6) * mm, "radius": 2.31 * mm});
            skCircle(sketch, "E13.9.8.0", {"center": v(25.4, 88.9) * mm, "radius": 2.31 * mm});
            skCircle(sketch, "E13.9.9.0", {"center": v(25.4, 76.2) * mm, "radius": 2.31 * mm});
            skCircle(sketch, "E13.10.0.0", {"center": v(38.1, 190.5) * mm, "radius": 2.31 * mm});
            skCircle(sketch, "E13.10.1.0", {"center": v(38.1, 177.8) * mm, "radius": 2.31 * mm});
            skCircle(sketch, "E13.10.2.0", {"center": v(38.1, 165.1) * mm, "radius": 2.31 * mm});
            skCircle(sketch, "E13.10.3.0", {"center": v(38.1, 152.4) * mm, "radius": 2.31 * mm});
            skCircle(sketch, "E13.10.4.0", {"center": v(38.1, 139.7) * mm, "radius": 2.31 * mm});
            skCircle(sketch, "E13.10.5.0", {"center": v(38.1, 127) * mm, "radius": 2.31 * mm});
            skCircle(sketch, "E13.10.6.0", {"center": v(38.1, 114.3) * mm, "radius": 2.31 * mm});
            skCircle(sketch, "E13.10.7.0", {"center": v(38.1, 101.6) * mm, "radius": 2.31 * mm});
            skCircle(sketch, "E13.10.8.0", {"center": v(38.1, 88.9) * mm, "radius": 2.31 * mm});
            skCircle(sketch, "E13.10.9.0", {"center": v(38.1, 76.2) * mm, "radius": 2.31 * mm});
            skCircle(sketch, "E13.10.10.0", {"center": v(38.1, 63.5) * mm, "radius": 2.31 * mm});
            skCircle(sketch, "E13.10.11.0", {"center": v(38.1, 50.8) * mm, "radius": 2.31 * mm});
            skCircle(sketch, "E13.10.12.0", {"center": v(38.1, 38.1) * mm, "radius": 2.31 * mm});
            skCircle(sketch, "E13.10.13.0", {"center": v(38.1, 25.4) * mm, "radius": 2.31 * mm});
            skCircle(sketch, "E13.10.14.0", {"center": v(38.1, 12.7) * mm, "radius": 2.31 * mm});
            skCircle(sketch, "E13.11.0.0", {"center": v(50.8, 190.5) * mm, "radius": 2.31 * mm});
            skCircle(sketch, "E13.11.1.0", {"center": v(50.8, 177.8) * mm, "radius": 2.31 * mm});
            skCircle(sketch, "E13.11.2.0", {"center": v(50.8, 165.1) * mm, "radius": 2.31 * mm});
            skCircle(sketch, "E13.11.3.0", {"center": v(50.8, 152.4) * mm, "radius": 2.31 * mm});
            skCircle(sketch, "E13.11.4.0", {"center": v(50.8, 139.7) * mm, "radius": 2.31 * mm});
            skCircle(sketch, "E13.11.5.0", {"center": v(50.8, 127) * mm, "radius": 2.31 * mm});
            skCircle(sketch, "E13.11.6.0", {"center": v(50.8, 114.3) * mm, "radius": 2.31 * mm});
            skCircle(sketch, "E13.11.7.0", {"center": v(50.8, 101.6) * mm, "radius": 2.31 * mm});
            skCircle(sketch, "E13.11.8.0", {"center": v(50.8, 88.9) * mm, "radius": 2.31 * mm});
            skCircle(sketch, "E13.11.9.0", {"center": v(50.8, 76.2) * mm, "radius": 2.31 * mm});
            skCircle(sketch, "E13.11.10.0", {"center": v(50.8, 63.5) * mm, "radius": 2.31 * mm});
            skCircle(sketch, "E13.11.11.0", {"center": v(50.8, 50.8) * mm, "radius": 2.31 * mm});
            skCircle(sketch, "E13.11.12.0", {"center": v(50.8, 38.1) * mm, "radius": 2.31 * mm});
            skCircle(sketch, "E13.11.13.0", {"center": v(50.8, 25.4) * mm, "radius": 2.31 * mm});
            skCircle(sketch, "E13.11.14.0", {"center": v(50.8, 12.7) * mm, "radius": 2.31 * mm});
            skCircle(sketch, "E13.12.0.0", {"center": v(63.5, 190.5) * mm, "radius": 2.31 * mm});
            skCircle(sketch, "E13.12.1.0", {"center": v(63.5, 177.8) * mm, "radius": 2.31 * mm});
            skCircle(sketch, "E13.12.2.0", {"center": v(63.5, 165.1) * mm, "radius": 2.31 * mm});
            skCircle(sketch, "E13.12.3.0", {"center": v(63.5, 152.4) * mm, "radius": 2.31 * mm});
            skCircle(sketch, "E13.12.4.0", {"center": v(63.5, 139.7) * mm, "radius": 2.31 * mm});
            skCircle(sketch, "E13.12.5.0", {"center": v(63.5, 127) * mm, "radius": 2.31 * mm});
            skCircle(sketch, "E13.12.6.0", {"center": v(63.5, 114.3) * mm, "radius": 2.31 * mm});
            skCircle(sketch, "E13.12.7.0", {"center": v(63.5, 101.6) * mm, "radius": 2.31 * mm});
            skCircle(sketch, "E13.12.8.0", {"center": v(63.5, 88.9) * mm, "radius": 2.31 * mm});
            skCircle(sketch, "E13.12.9.0", {"center": v(63.5, 76.2) * mm, "radius": 2.31 * mm});
            skCircle(sketch, "E13.12.10.0", {"center": v(63.5, 63.5) * mm, "radius": 2.31 * mm});
            skCircle(sketch, "E13.12.11.0", {"center": v(63.5, 50.8) * mm, "radius": 2.31 * mm});
            skCircle(sketch, "E13.12.12.0", {"center": v(63.5, 38.1) * mm, "radius": 2.31 * mm});
            skCircle(sketch, "E13.12.13.0", {"center": v(63.5, 25.4) * mm, "radius": 2.31 * mm});
            skCircle(sketch, "E13.12.14.0", {"center": v(63.5, 12.7) * mm, "radius": 2.31 * mm});
            skCircle(sketch, "E13.13.0.0", {"center": v(76.2, 190.5) * mm, "radius": 2.31 * mm});
            skCircle(sketch, "E13.13.1.0", {"center": v(76.2, 177.8) * mm, "radius": 2.31 * mm});
            skCircle(sketch, "E13.13.2.0", {"center": v(76.2, 165.1) * mm, "radius": 2.31 * mm});
            skCircle(sketch, "E13.13.3.0", {"center": v(76.2, 152.4) * mm, "radius": 2.31 * mm});
            skCircle(sketch, "E13.13.4.0", {"center": v(76.2, 139.7) * mm, "radius": 2.31 * mm});
            skCircle(sketch, "E13.13.5.0", {"center": v(76.2, 127) * mm, "radius": 2.31 * mm});
            skCircle(sketch, "E13.13.6.0", {"center": v(76.2, 114.3) * mm, "radius": 2.31 * mm});
            skCircle(sketch, "E13.13.7.0", {"center": v(76.2, 101.6) * mm, "radius": 2.31 * mm});
            skCircle(sketch, "E13.13.8.0", {"center": v(76.2, 88.9) * mm, "radius": 2.31 * mm});
            skCircle(sketch, "E13.13.9.0", {"center": v(76.2, 76.2) * mm, "radius": 2.31 * mm});
            skCircle(sketch, "E13.13.10.0", {"center": v(76.2, 63.5) * mm, "radius": 2.31 * mm});
            skCircle(sketch, "E13.13.11.0", {"center": v(76.2, 50.8) * mm, "radius": 2.31 * mm});
            skCircle(sketch, "E13.13.12.0", {"center": v(76.2, 38.1) * mm, "radius": 2.31 * mm});
            skCircle(sketch, "E13.13.13.0", {"center": v(76.2, 25.4) * mm, "radius": 2.31 * mm});
            skCircle(sketch, "E13.13.14.0", {"center": v(76.2, 12.7) * mm, "radius": 2.31 * mm});
            skCircle(sketch, "E13.14.0.0", {"center": v(88.9, 190.5) * mm, "radius": 2.31 * mm});
            skCircle(sketch, "E13.14.1.0", {"center": v(88.9, 177.8) * mm, "radius": 2.31 * mm});
            skCircle(sketch, "E13.14.2.0", {"center": v(88.9, 165.1) * mm, "radius": 2.31 * mm});
            skCircle(sketch, "E13.14.3.0", {"center": v(88.9, 152.4) * mm, "radius": 2.31 * mm});
            skCircle(sketch, "E13.14.4.0", {"center": v(88.9, 139.7) * mm, "radius": 2.31 * mm});
            skCircle(sketch, "E13.14.5.0", {"center": v(88.9, 127) * mm, "radius": 2.31 * mm});
            skCircle(sketch, "E13.14.6.0", {"center": v(88.9, 114.3) * mm, "radius": 2.31 * mm});
            skCircle(sketch, "E13.14.7.0", {"center": v(88.9, 101.6) * mm, "radius": 2.31 * mm});
            skCircle(sketch, "E13.14.8.0", {"center": v(88.9, 88.9) * mm, "radius": 2.31 * mm});
            skCircle(sketch, "E13.14.9.0", {"center": v(88.9, 76.2) * mm, "radius": 2.31 * mm});
            skCircle(sketch, "E13.14.10.0", {"center": v(88.9, 63.5) * mm, "radius": 2.31 * mm});
            skCircle(sketch, "E13.14.11.0", {"center": v(88.9, 50.8) * mm, "radius": 2.31 * mm});
            skCircle(sketch, "E13.14.12.0", {"center": v(88.9, 38.1) * mm, "radius": 2.31 * mm});
            skCircle(sketch, "E13.14.13.0", {"center": v(88.9, 25.4) * mm, "radius": 2.31 * mm});
            skCircle(sketch, "E13.14.14.0", {"center": v(88.9, 12.7) * mm, "radius": 2.31 * mm});
            skLineSegment(sketch, "E13.direction1", {"start": v(-88.9, 190.5) * mm, "end": v(-76.2, 190.5) * mm, "construction": true});
            skLineSegment(sketch, "E13.direction2", {"start": v(-88.9, 190.5) * mm, "end": v(-88.9, 177.8) * mm, "construction": true});
            skLineSegment(sketch, "E14", {"start": v(-26.67, 4.04) * mm, "end": v(-26.67, 72.62) * mm, "construction": true});
            skCircle(sketch, "E15", {"center": v(24.13, 18) * mm, "radius": 1.59 * mm});
            skCircle(sketch, "E16", {"center": v(-24.13, 19.28) * mm, "radius": 1.59 * mm});
            skCircle(sketch, "E17", {"center": v(-8.9, 70.08) * mm, "radius": 1.59 * mm});
            skCircle(sketch, "E18", {"center": v(19.05, 70.08) * mm, "radius": 1.59 * mm});
            skLineSegment(sketch, "E19", {"start": v(-26.67, 72.62) * mm, "end": v(26.67, 72.62) * mm, "construction": true});
            skLineSegment(sketch, "E20", {"start": v(26.67, 72.62) * mm, "end": v(26.67, 4.04) * mm, "construction": true});
            skSolve(sketch);
        }
        {
            var Q0;
            Q0 = qSketchRegion(id + "F0", true);
            extrude(context, id + "F1", {"entities" : qUnion([Q0]), "depth" : 3.17 * mm});
        }
    });
